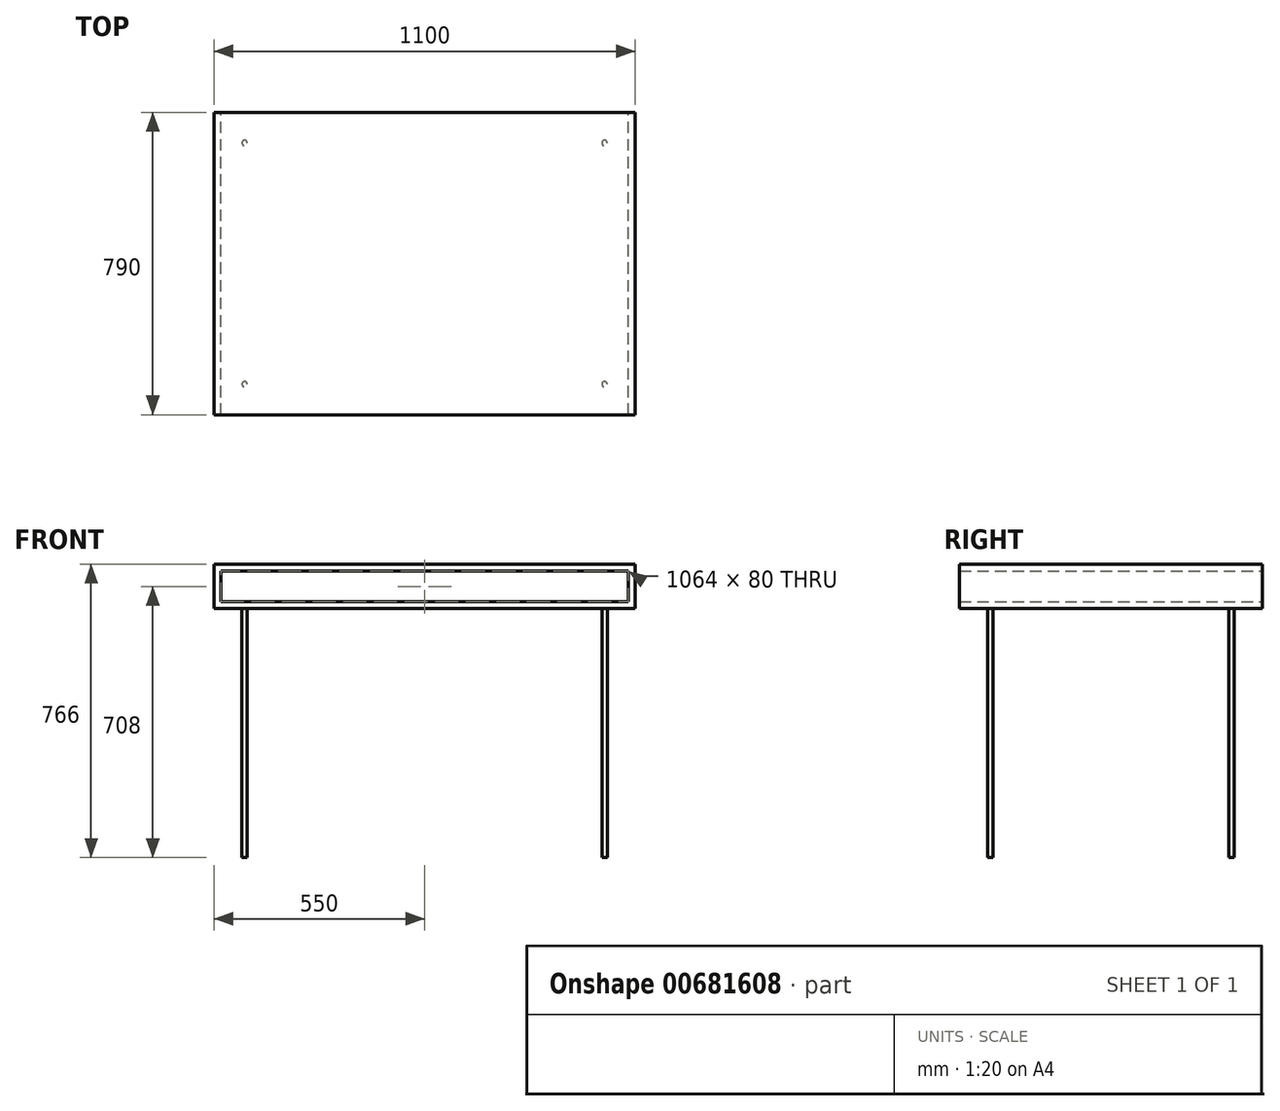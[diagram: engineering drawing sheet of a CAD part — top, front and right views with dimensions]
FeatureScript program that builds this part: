
annotation { "Feature Type Name" : "Feature", "Feature Type Description" : "" }
export const myFeature = defineFeature(function(context is Context, id is Id, definition is map)
    precondition{}
    {
        {
            var Q0;
            Q0=qCreatedBy(makeId("Front.planeOp"),FACE);
            var sketch = newSketch(context, id + "F0", { "sketchPlane" : qUnion([Q0])});
            skLineSegment(sketch, "E0.bottom", {"start": v(-550, 0) * mm, "end": v(550, 0) * mm});
            skLineSegment(sketch, "E0.top", {"start": v(-550, 116) * mm, "end": v(550, 116) * mm});
            skLineSegment(sketch, "E0.left", {"start": v(-550, 0) * mm, "end": v(-550, 116) * mm});
            skLineSegment(sketch, "E0.right", {"start": v(550, 0) * mm, "end": v(550, 116) * mm});
            skPoint(sketch, "E1", {"position": v(0, 0) * mm});
            skLineSegment(sketch, "E2.0", {"start": v(532, 18) * mm, "end": v(532, 98) * mm});
            skLineSegment(sketch, "E2.1", {"start": v(-532, 18) * mm, "end": v(532, 18) * mm});
            skLineSegment(sketch, "E2.2", {"start": v(-532, 18) * mm, "end": v(-532, 98) * mm});
            skLineSegment(sketch, "E2.3", {"start": v(-532, 98) * mm, "end": v(532, 98) * mm});
            skLineSegment(sketch, "E3", {"start": v(532, 98) * mm, "end": v(550, 116) * mm});
            skLineSegment(sketch, "E4", {"start": v(532, 18) * mm, "end": v(550, 18) * mm});
            skLineSegment(sketch, "E5", {"start": v(-532, 18) * mm, "end": v(-550, 0) * mm});
            skLineSegment(sketch, "E6", {"start": v(-532, 98) * mm, "end": v(-550, 98) * mm});
            skSolve(sketch);
        }
        {
            var Q0;
            Q0=makeQuery(id+"F0.imprint","IMPRINT",FACE,{"disambiguationData":[TD([[makeQuery(id+"F0.imprint","IMPRINT",EDGE,{"derivedFrom":sQuery(id+"F0.wireOp",EDGE,"E0.bottom")}),1.0]])]});
            var Q1;
            Q1=makeQuery(id+"F0.imprint","IMPRINT",FACE,{"disambiguationData":[TD([[makeQuery(id+"F0.imprint","IMPRINT",EDGE,{"derivedFrom":sQuery(id+"F0.wireOp",EDGE,"E2.0")}),-1.0]])]});
            var Q2;
            {var subQ1=sQuery(id+"F0.wireOp",EDGE,"E0.top");Q2=makeQuery(id+"F0.imprint","IMPRINT",FACE,{"disambiguationData":[TD([[makeQuery(id+"F0.imprint","IMPRINT",EDGE,{"derivedFrom":subQ1}),-1.0]])]});}
            var Q3;
            Q3=makeQuery(id+"F0.imprint","IMPRINT",FACE,{"disambiguationData":[TD([[makeQuery(id+"F0.imprint","IMPRINT",EDGE,{"derivedFrom":sQuery(id+"F0.wireOp",EDGE,"E2.2")}),1.0]])]});
            extrude(context, id + "F1", {"entities" : qUnion([Q0, Q1, Q2, Q3]), "depth" : 790 * mm, "offsetDistance" : 25 * mm});
        }
        {
            var Q0;
            Q0=makeQuery(id+"F1.opExtrude","SWEPT_FACE",FACE,{"disambiguationData":[OSD([sQuery(id+"F0.wireOp",EDGE,"E0.bottom")])]});
            var sketch = newSketch(context, id + "F2", { "sketchPlane" : qUnion([Q0])});
            skLineSegment(sketch, "E7", {"start": v(-650.42, 395) * mm, "end": v(637.73, 395) * mm, "construction": true});
            skPoint(sketch, "E7.startSnap0", {"position": v(-550, 395) * mm});
            skLineSegment(sketch, "E8", {"start": v(0, -55.7) * mm, "end": v(0, 743.64) * mm, "construction": true});
            skPoint(sketch, "E8.endSnap0", {"position": v(0, 790) * mm});
            skCircle(sketch, "E9", {"center": v(-470, 80) * mm, "radius": 7 * mm});
            skCircle(sketch, "E10.MirrorC", {"center": v(-470, 710) * mm, "radius": 7 * mm});
            skCircle(sketch, "E11.MirrorC", {"center": v(470, 80) * mm, "radius": 7 * mm});
            skCircle(sketch, "E12.MirrorC", {"center": v(470, 710) * mm, "radius": 7 * mm});
            skSolve(sketch);
        }
        {
            var Q0;
            Q0 = qSketchRegion(id + "F2", true);
            extrude(context, id + "F3", {"entities" : qUnion([Q0]), "depth" : 650 * mm, "offsetDistance" : 25 * mm});
        }
    });
